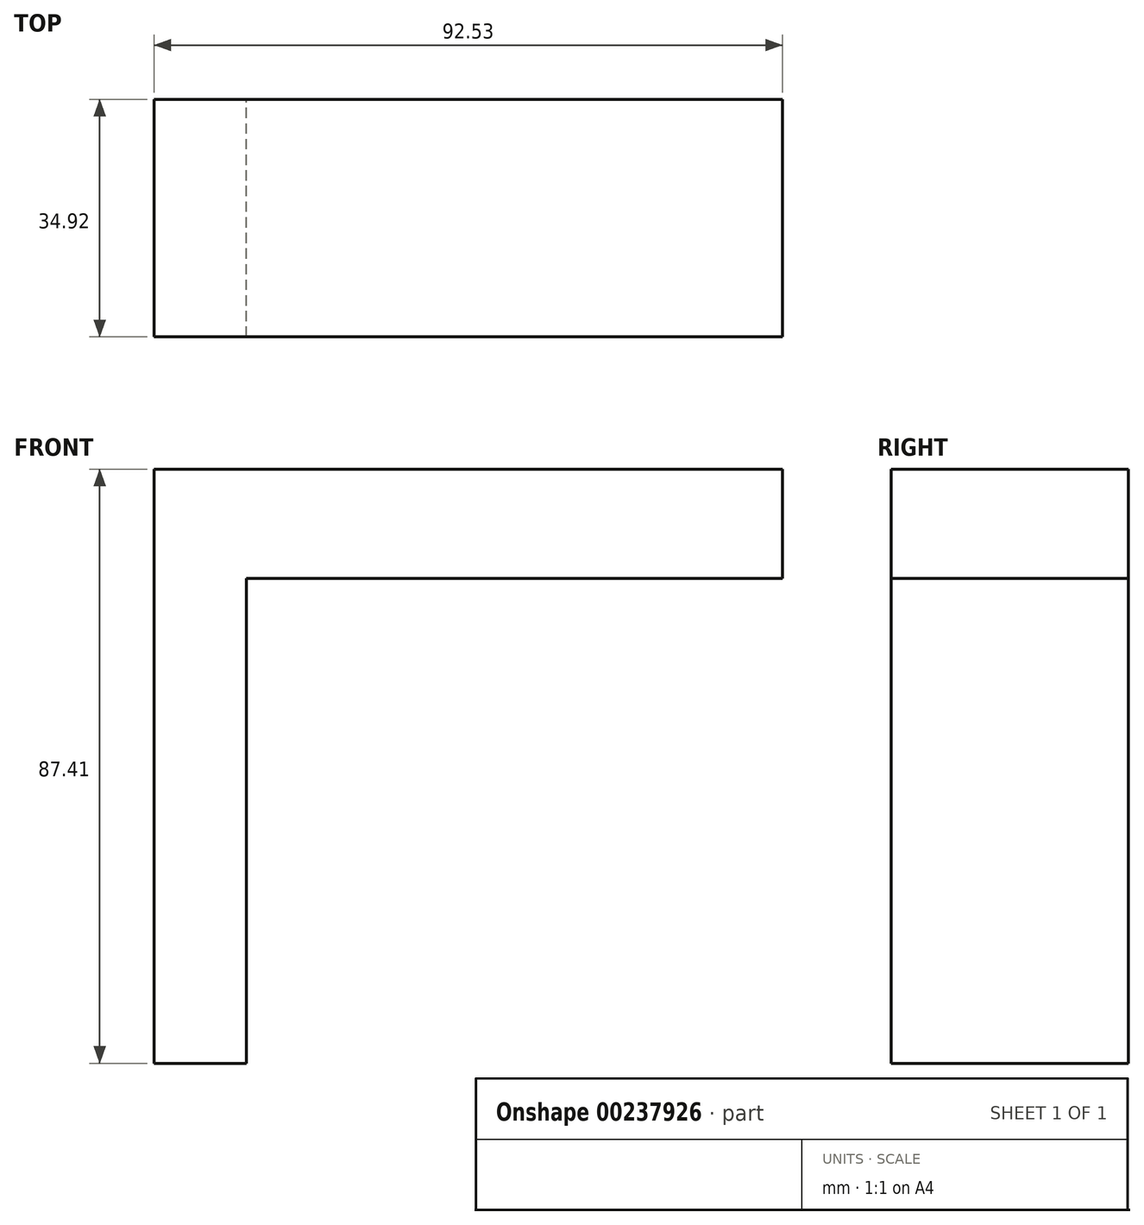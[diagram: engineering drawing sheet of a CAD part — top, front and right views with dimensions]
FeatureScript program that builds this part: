
annotation { "Feature Type Name" : "Feature", "Feature Type Description" : "" }
export const myFeature = defineFeature(function(context is Context, id is Id, definition is map)
    precondition{}
    {
        {
            var Q0;
            Q0=qCreatedBy(makeId("Front.planeOp"),FACE);
            var sketch = newSketch(context, id + "F0", { "sketchPlane" : qUnion([Q0])});
            skLineSegment(sketch, "E0.bottom", {"start": v(-78.9, 0) * mm, "end": v(-92.53, 0) * mm});
            skLineSegment(sketch, "E0.top", {"start": v(-78.9, 87.41) * mm, "end": v(-92.53, 87.41) * mm});
            skLineSegment(sketch, "E0.left", {"start": v(-78.9, 0) * mm, "end": v(-78.9, 87.41) * mm});
            skLineSegment(sketch, "E0.right", {"start": v(-92.53, 0) * mm, "end": v(-92.53, 87.41) * mm});
            skLineSegment(sketch, "E1.bottom", {"start": v(-78.9, 71.34) * mm, "end": v(0, 71.34) * mm});
            skLineSegment(sketch, "E1.top", {"start": v(-78.9, 87.41) * mm, "end": v(0, 87.41) * mm});
            skLineSegment(sketch, "E1.left", {"start": v(-78.9, 71.34) * mm, "end": v(-78.9, 87.41) * mm});
            skLineSegment(sketch, "E1.right", {"start": v(0, 71.34) * mm, "end": v(0, 87.41) * mm});
            skSolve(sketch);
        }
        {
            var Q0;
            Q0=makeQuery(id+"F0.imprint","IMPRINT",FACE,{"disambiguationData":[TD([[makeQuery(id+"F0.imprint","IMPRINT",EDGE,{"derivedFrom":sQuery(id+"F0.wireOp",EDGE,"E0.bottom")}),-1.0]])]});
            var Q1;
            Q1=makeQuery(id+"F0.imprint","IMPRINT",FACE,{"disambiguationData":[TD([[makeQuery(id+"F0.imprint","IMPRINT",EDGE,{"derivedFrom":sQuery(id+"F0.wireOp",EDGE,"E1.bottom")}),1.0]])]});
            extrude(context, id + "F1", {"entities" : qUnion([Q0, Q1]), "depth" : 25.4 * mm});
        }
        {
            var Q0;
            Q0=makeQuery(id+"F1.opExtrude","CAP_FACE",FACE,{"disambiguationData":[OSD([sQuery(id+"F0.wireOp",EDGE,"E0.bottom"),sQuery(id+"F0.wireOp",EDGE,"E0.top"),sQuery(id+"F0.wireOp",EDGE,"E0.left"),sQuery(id+"F0.wireOp",EDGE,"E0.right"),sQuery(id+"F0.wireOp",EDGE,"E1.bottom"),sQuery(id+"F0.wireOp",EDGE,"E1.top"),sQuery(id+"F0.wireOp",EDGE,"E1.right")])],"isStart":false});
            extrude(context, id + "F2", {"entities" : qUnion([Q0]), "operationType" : NewBodyOperationType.ADD, "endBound" : BoundingType.SYMMETRIC, "depth" : 19.05 * mm});
        }
    });
